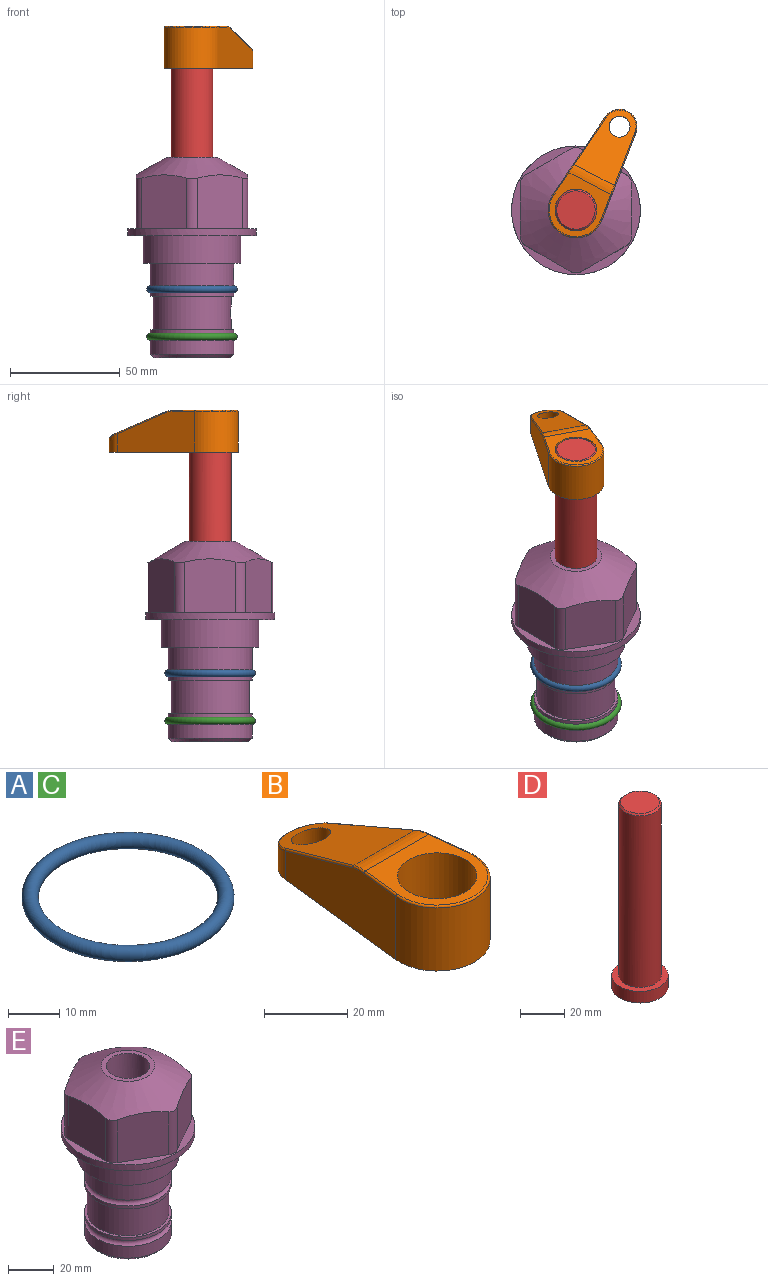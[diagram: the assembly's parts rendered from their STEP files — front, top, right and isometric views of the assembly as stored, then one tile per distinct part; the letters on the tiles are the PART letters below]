
ASSEMBLY  parts=5 mates=2
PART A: 1 faces, bbox 44.7x44.7x3.2 mm
  f0: torus R=19.05mm, axis (0,0,1), area 1193.9mm2
PART B: 44 faces, bbox 27.5x64.5x19.1 mm
  f0: plane 2.3x0.95mm, normal (0,0,-1), area 1mm2, adj f25,f30,f34
  f1: plane 63.5x25.4mm, normal (0,0,-1), area 561.7mm2, adj f2,f3,f4,f5,f6,f7,f19,f20
  f2: cylinder r=12.7mm len=25.4mm, axis (0,0,-1), area 792.2mm2, adj f1,f3,f5,f13
  f3: plane 42.33x18.54mm, normal (0.99,0.11,0), area 647mm2, adj f1,f2,f4,f11,f12,f14
  f4: cylinder r=7.94mm len=15.78mm, axis (0,0,-1), area 158.6mm2, adj f1,f3,f5,f16
  f5: plane 42.33x18.54mm, normal (-0.99,0.11,0), area 647mm2, adj f1,f2,f4,f15,f17,f18
  f6: cylinder r=9.53mm len=19.05mm, axis (0,0,-1), area 1140.1mm2, adj f1,f8
  f7: cylinder r=4.76mm len=10.98mm, axis (0,0,-1), area 276.1mm2, adj f1,f9
  f8: plane 25.83x24.38mm, normal (0,0,1), area 262.2mm2, adj f6,f10,f11,f13,f15
  f9: plane 32.49x20.55mm, normal (0,0.34,0.94), area 489.9mm2, adj f7,f10,f14,f16,f18
  f10: cylinder r=12.7mm len=21.49mm, axis (-1,0,0), area 93.2mm2, adj f8,f9,f12,f17
  f11: cylinder r=0.51mm len=12.34mm, axis (0.11,-0.99,0), area 9.9mm2, adj f3,f8,f12,f13
  f12: bspline ~7.62x1.64mm, area 3.5mm2, adj f3,f10,f11,f14
  f13: torus R=12.19mm, axis (0,0,1), area 33.6mm2, adj f2,f8,f11,f15
  f14: cylinder r=0.51mm len=26.01mm, axis (0.1,-0.93,0.34), area 21.6mm2, adj f3,f9,f12,f16
  f15: cylinder r=0.51mm len=12.34mm, axis (0.11,0.99,0), area 9.9mm2, adj f5,f8,f13,f17
  f16: bspline ~15.78x7.05mm, area 15.7mm2, adj f4,f9,f14,f18
  f17: bspline ~7.62x1.64mm, area 3.5mm2, adj f5,f10,f15,f18
  f18: cylinder r=0.51mm len=26.01mm, axis (0.1,0.93,-0.34), area 21.6mm2, adj f5,f9,f16,f17
  f19: plane 21.6x14.29mm, normal (-0.99,-0.11,0), area 242.6mm2, adj f1,f26,f28,f34,f36,f38
  f20: plane 21.6x14.29mm, normal (0.99,-0.11,0), area 242.6mm2, adj f1,f27,f29,f37,f39,f41
  f21: cylinder r=12.7mm len=14.29mm, axis (0,0,-1), area 173.2mm2, adj f1,f26,f27,f30,f31,f33
  f22: cylinder r=7.94mm len=7.63mm, axis (0,0,-1), area 53.8mm2, adj f1,f28,f29,f42
  f23: plane 2.3x0.95mm, normal (0,0,-1), area 1mm2, adj f25,f33,f37
  f24: plane 17.94x12.32mm, normal (0,-0.34,-0.94), area 191.2mm2, adj f25,f38,f41,f42
  f25: cylinder r=9.53mm len=12.93mm, axis (-1,0,0), area 37.5mm2, adj f0,f23,f24,f31,f36,f39
  f26: cylinder r=1.59mm len=14.29mm, axis (0,0,-1), area 49mm2, adj f1,f19,f21,f32
  f27: cylinder r=1.59mm len=14.29mm, axis (0,0,-1), area 49mm2, adj f1,f20,f21,f35
  f28: cylinder r=1.59mm len=7.28mm, axis (0,0,-1), area 22.1mm2, adj f1,f19,f22,f40
  f29: cylinder r=1.59mm len=7.28mm, axis (0,0,-1), area 22.1mm2, adj f1,f20,f22,f43
  f30: torus R=14.29mm, axis (0,0,1), area 5.8mm2, adj f0,f21,f31,f32
  f31: bspline ~11.06x2.73mm, area 20.8mm2, adj f21,f25,f30,f33
  f32: sphere r=1.59mm, area 5.4mm2, adj f26,f30,f34
  f33: torus R=14.29mm, axis (0,0,1), area 5.8mm2, adj f21,f23,f31,f35
  f34: cylinder r=1.59mm len=1.68mm, axis (-0.11,0.99,0), area 2.4mm2, adj f0,f19,f32,f36
  f35: sphere r=1.59mm, area 5.4mm2, adj f27,f33,f37
  f36: bspline ~5.82x2.33mm, area 7.7mm2, adj f19,f25,f34,f38
  f37: cylinder r=1.59mm len=1.68mm, axis (0.11,0.99,0), area 2.4mm2, adj f20,f23,f35,f39
  f38: cylinder r=1.59mm len=18.33mm, axis (0.1,-0.93,0.34), area 46.7mm2, adj f19,f24,f36,f40
  f39: bspline ~5.82x2.33mm, area 7.7mm2, adj f20,f25,f37,f41
  f40: sphere r=1.59mm, area 3.6mm2, adj f28,f38,f42
  f41: cylinder r=1.59mm len=18.33mm, axis (0.1,0.93,-0.34), area 46.7mm2, adj f20,f24,f39,f43
  f42: bspline ~8.31x1.84mm, area 15.3mm2, adj f22,f24,f40,f43
  f43: sphere r=1.59mm, area 3.6mm2, adj f29,f41,f42
PART C: same geometry as A
PART D: 6 faces, bbox 25.4x25.4x101.6 mm
  f0: plane 17.46x17.46mm, normal (0,0,1), area 239.5mm2, adj f5
  f1: plane 25.4x25.4mm, normal (0,0,-1), area 506.7mm2, adj f2
  f2: cylinder r=12.7mm len=25.4mm, axis (0,0,1), area 506.7mm2, adj f1,f3
  f3: plane 25.4x25.4mm, normal (0,0,1), area 221.7mm2, adj f2,f4
  f4: cylinder r=9.53mm len=94.46mm, axis (0,0,1), area 5653mm2, adj f3,f5
  f5: cone r=8.73mm half-angle=45deg, axis (0,0,-1), area 64.4mm2, adj f0,f4
PART E: 36 faces, bbox 58.7x58.7x91.2 mm
  f0: cylinder r=17.78mm len=35.56mm, axis (0,0,1), area 1670.8mm2, adj f23,f24,f31
  f1: cylinder r=19.05mm len=38.1mm, axis (0,0,1), area 1191.9mm2, adj f26,f27,f30
  f2: plane 58.66x58.66mm, normal (0,0,-1), area 1150.6mm2, adj f3,f28
  f3: cylinder r=29.33mm len=58.66mm, axis (0,0,-1), area 585.1mm2, adj f2,f4
  f4: plane 58.66x58.66mm, normal (0,0,1), area 475.9mm2, adj f3,f5,f6,f7,f8,f9,f10,f11
  f5: plane 24.5x20.32mm, normal (-0.5,0.87,0), area 562.8mm2, adj f4,f15,f16,f17
  f6: plane 24.5x20.32mm, normal (0.5,0.87,0), area 562.8mm2, adj f4,f14,f15,f17
  f7: plane 24.5x23.48mm, normal (1,0,0), area 562.8mm2, adj f4,f13,f14,f17
  f8: plane 24.5x20.32mm, normal (0.5,-0.87,0), area 562.8mm2, adj f4,f12,f13,f17
  f9: plane 24.5x20.32mm, normal (-0.5,-0.87,0), area 562.8mm2, adj f4,f11,f12,f17
  f10: plane 24.5x23.48mm, normal (-1,0,0), area 562.8mm2, adj f4,f11,f16,f17
  f11: cylinder r=5.08mm len=23.01mm, axis (0,0,-1), area 121.2mm2, adj f4,f9,f10,f17
  f12: cylinder r=5.08mm len=23.01mm, axis (0,0,-1), area 121.2mm2, adj f4,f8,f9,f17
  f13: cylinder r=5.08mm len=23.01mm, axis (0,0,-1), area 121.2mm2, adj f4,f7,f8,f17
  f14: cylinder r=5.08mm len=23.01mm, axis (0,0,-1), area 121.2mm2, adj f4,f6,f7,f17
  f15: cylinder r=5.08mm len=23.01mm, axis (0,0,-1), area 121.2mm2, adj f4,f5,f6,f17
  f16: cylinder r=5.08mm len=23.01mm, axis (0,0,-1), area 121.2mm2, adj f4,f5,f10,f17
  f17: cone r=11.73mm half-angle=60deg, axis (0,0,-1), area 2071.8mm2, adj f5,f6,f7,f8,f9,f10,f11,f12
  f18: plane 23.46x23.46mm, normal (0,0,1), area 147.4mm2, adj f17,f35
  f19: plane 34.93x34.93mm, normal (0,0,-1), area 958mm2, adj f29
  f20: cylinder r=19.05mm len=38.1mm, axis (0,0,1), area 760.1mm2, adj f21,f29
  f21: torus R=19.05mm, axis (0,0,1), area 565.3mm2, adj f20,f22
  f22: cylinder r=19.05mm len=38.1mm, axis (0,0,1), area 190mm2, adj f21,f23
  f23: plane 38.1x38.1mm, normal (0,0,1), area 146.9mm2, adj f0,f22
  f24: plane 38.1x38.1mm, normal (0,0,-1), area 146.9mm2, adj f0,f25
  f25: cylinder r=19.05mm len=38.1mm, axis (0,0,1), area 190mm2, adj f24,f26
  f26: torus R=19.05mm, axis (0,0,1), area 565.3mm2, adj f1,f25
  f27: plane 44.45x44.45mm, normal (0,0,-1), area 411.7mm2, adj f1,f28
  f28: cylinder r=22.23mm len=44.45mm, axis (0,0,1), area 1773.5mm2, adj f2,f27
  f29: cone r=19.05mm half-angle=45deg, axis (0,0,1), area 257.5mm2, adj f19,f20
  f30: cylinder r=3.17mm len=6.75mm, axis (-1,0,0), area 128mm2, adj f1,f33
  f31: cylinder r=3.17mm len=6.35mm, axis (-1,0,0), area 102.5mm2, adj f0,f33
  f32: plane 25.4x25.4mm, normal (0,0,1), area 506.7mm2, adj f33
  f33: cylinder r=12.7mm len=66.42mm, axis (0,0,-1), area 5236.2mm2, adj f30,f31,f32,f34
  f34: cone r=9.53mm half-angle=30deg, axis (0,0,-1), area 443.4mm2, adj f33,f35
  f35: cylinder r=9.53mm len=19.05mm, axis (0,0,-1), area 849mm2, adj f18,f34
PLACE A t=(-0.59,-2.32,-2.96)mm
PLACE B rot(axis=(0,0,-1),27.6deg) t=(-0.59,-2.32,73.3)mm
PLACE C t=(-0.59,-2.32,-24.55)mm
PLACE D rot(axis=(0,0,-1),27.6deg) t=(-0.59,-2.32,18.69)mm
PLACE E t=(-0.59,-2.32,-2.96)mm
MATE fastened B.f2 <-> D.f2  axis (0,0,-1) through (-0.59,-2.32,92.35)mm
MATE cylindrical D.f2 <-> E.f0  axis (0,0,1) through (-0.59,-2.32,44.33)mm
